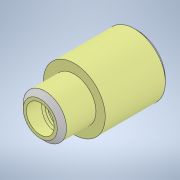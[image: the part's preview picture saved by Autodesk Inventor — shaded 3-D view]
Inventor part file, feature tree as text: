
AUTODESK INVENTOR PART (.ipt)
format: ipt  version: 2021.2 (Build 252289000, 289)  size: 534,016 bytes
history: native  units: mm
features: other x4, chamfer x2
ambient origin geometry x8: Origin, YZ Plane, XZ Plane, XY Plane, X Axis, Y Axis, Z Axis, Center Point
bodies: Body1 (feature_tree)
feature tree (6):
  other  "Твёрдое тело.ipt"
  chamfer  "Фаска1"  Distance=10.0mm
  chamfer  "Фаска2"  Distance=0.5mm Angle=45.0deg
  other  "Вал насадка 1::Твёрдое тело.ipt"
  other  "Элемент создания тегов1"
  other  "Твердое тело1"
